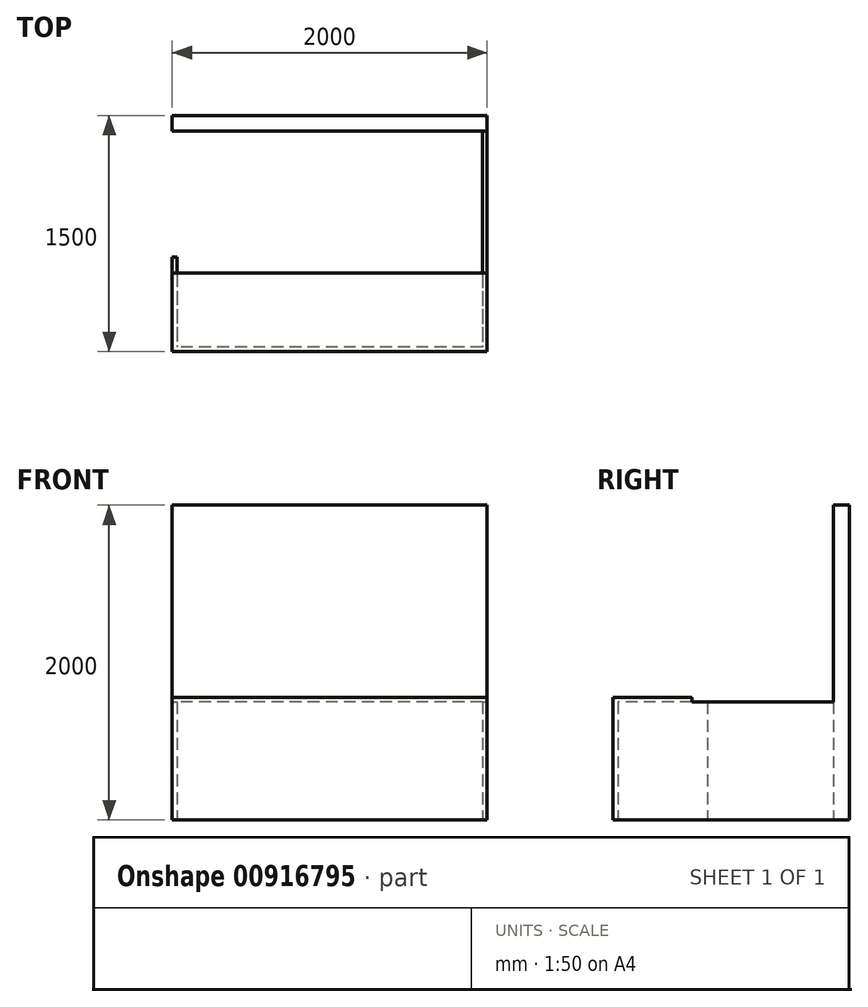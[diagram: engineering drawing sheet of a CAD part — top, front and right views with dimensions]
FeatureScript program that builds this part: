
annotation { "Feature Type Name" : "Feature", "Feature Type Description" : "" }
export const myFeature = defineFeature(function(context is Context, id is Id, definition is map)
    precondition{}
    {
        {
            var Q0;
            Q0=qCreatedBy(makeId("Top.planeOp"),FACE);
            var sketch = newSketch(context, id + "F0", { "sketchPlane" : qUnion([Q0])});
            skLineSegment(sketch, "E0.bottom", {"start": v(1000, 750) * mm, "end": v(-1000, 750) * mm});
            skLineSegment(sketch, "E0.top", {"start": v(1000, -750) * mm, "end": v(-1000, -750) * mm});
            skLineSegment(sketch, "E0.left", {"start": v(1000, 750) * mm, "end": v(1000, -750) * mm});
            skLineSegment(sketch, "E0.right", {"start": v(-1000, 750) * mm, "end": v(-1000, -750) * mm});
            skPoint(sketch, "E0.middle", {"position": v(0, 0) * mm});
            skLineSegment(sketch, "E1", {"start": v(-1000, -250) * mm, "end": v(1000, -250) * mm});
            skLineSegment(sketch, "E2", {"start": v(-1000, 650) * mm, "end": v(1000, 650) * mm});
            skSolve(sketch);
        }
        {
            var Q0;
            Q0=qCreatedBy(makeId("Top.planeOp"),FACE);
            var sketch = newSketch(context, id + "F1", { "sketchPlane" : qUnion([Q0])});
            skLineSegment(sketch, "E3.0", {"start": v(1000, 750) * mm, "end": v(-1000, 750) * mm});
            skLineSegment(sketch, "E3.1", {"start": v(-1000, 650) * mm, "end": v(1000, 650) * mm});
            skLineSegment(sketch, "E3.2", {"start": v(1000, 750) * mm, "end": v(1000, 650) * mm});
            skLineSegment(sketch, "E3.3", {"start": v(-1000, 750) * mm, "end": v(-1000, 650) * mm});
            skPoint(sketch, "E4.orphan", {"position": v(-1000, -750) * mm});
            skPoint(sketch, "E5.orphan", {"position": v(1000, -750) * mm});
            skSolve(sketch);
        }
        {
            var Q0;
            Q0 = qSketchRegion(id + "F1", true);
            extrude(context, id + "F2", {"entities" : qUnion([Q0]), "depth" : 2000 * mm, "offsetDistance" : 25 * mm});
        }
        {
            var Q0;
            Q0=qCreatedBy(makeId("Top.planeOp"),FACE);
            var sketch = newSketch(context, id + "F3", { "sketchPlane" : qUnion([Q0])});
            skLineSegment(sketch, "E6.0", {"start": v(1000, 750) * mm, "end": v(1000, -750) * mm});
            skLineSegment(sketch, "E6.1", {"start": v(1000, -750) * mm, "end": v(-1000, -750) * mm});
            skLineSegment(sketch, "E6.2", {"start": v(-1000, -150) * mm, "end": v(-1000, -750) * mm});
            skLineSegment(sketch, "E7.0", {"start": v(-970, -150) * mm, "end": v(-970, -720) * mm});
            skLineSegment(sketch, "E7.1", {"start": v(970, -720) * mm, "end": v(-970, -720) * mm});
            skLineSegment(sketch, "E7.2", {"start": v(970, 750) * mm, "end": v(970, -720) * mm});
            skLineSegment(sketch, "E8", {"start": v(1000, 750) * mm, "end": v(970, 750) * mm});
            skLineSegment(sketch, "E9", {"start": v(-1000, -150) * mm, "end": v(-970, -150) * mm});
            skSolve(sketch);
        }
        {
            var Q0;
            Q0 = qSketchRegion(id + "F3", true);
            extrude(context, id + "F4", {"entities" : qUnion([Q0]), "operationType" : NewBodyOperationType.ADD, "depth" : 750 * mm, "offsetDistance" : 25 * mm});
        }
        {
            var Q0;
            Q0=makeQuery(id+"F4.opExtrude","CAP_FACE",FACE,{"disambiguationData":[OSD([sQuery(id+"F3.wireOp",EDGE,"E6.0"),sQuery(id+"F3.wireOp",EDGE,"E6.1"),sQuery(id+"F3.wireOp",EDGE,"E6.2"),sQuery(id+"F3.wireOp",EDGE,"E7.0"),sQuery(id+"F3.wireOp",EDGE,"E7.1"),sQuery(id+"F3.wireOp",EDGE,"E7.2"),sQuery(id+"F3.wireOp",EDGE,"E8"),sQuery(id+"F3.wireOp",EDGE,"E9")])],"isStart":false});
            var sketch = newSketch(context, id + "F5", { "sketchPlane" : qUnion([Q0])});
            skLineSegment(sketch, "E10.0", {"start": v(-1000, -250) * mm, "end": v(1000, -250) * mm});
            skLineSegment(sketch, "E10.1", {"start": v(1000, -250) * mm, "end": v(1000, -750) * mm});
            skLineSegment(sketch, "E10.2", {"start": v(1000, -750) * mm, "end": v(-1000, -750) * mm});
            skLineSegment(sketch, "E10.3", {"start": v(-1000, -250) * mm, "end": v(-1000, -750) * mm});
            skPoint(sketch, "E11.orphan", {"position": v(-1000, 750) * mm});
            skPoint(sketch, "E12.orphan", {"position": v(1000, 750) * mm});
            skSolve(sketch);
        }
        {
            var Q0;
            Q0 = qSketchRegion(id + "F5", true);
            extrude(context, id + "F6", {"entities" : qUnion([Q0]), "operationType" : NewBodyOperationType.ADD, "depth" : 30 * mm, "offsetDistance" : 25 * mm});
        }
        {
            var Q0;
            Q0=makeQuery(id+"F2.opExtrude","SWEPT_BODY",BODY,{"disambiguationData":[OSD([sQuery(id+"F1.wireOp",EDGE,"E3.0"),sQuery(id+"F1.wireOp",EDGE,"E3.1"),sQuery(id+"F1.wireOp",EDGE,"E3.2"),sQuery(id+"F1.wireOp",EDGE,"E3.3")])]});
            var Q1;
            Q1=qCreatedBy(makeId("Right.planeOp"),FACE);
            mirror(context, id + "F7", {"entities" : qUnion([Q0]), "mirrorPlane" : qUnion([Q1])});
        }
        {
            var Q0;
            Q0=makeQuery(id+"F7.opPattern","COPY",BODY,{"derivedFrom":makeQuery(id+"F2.opExtrude","SWEPT_BODY",BODY,{"disambiguationData":[OSD([sQuery(id+"F1.wireOp",EDGE,"E3.0"),sQuery(id+"F1.wireOp",EDGE,"E3.1"),sQuery(id+"F1.wireOp",EDGE,"E3.2"),sQuery(id+"F1.wireOp",EDGE,"E3.3")])]}),"instanceName":"1"});
            deleteBodies(context, id + "F8", {"entities" : qUnion([Q0])});
        }
    });
